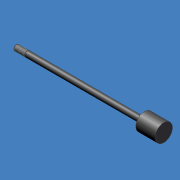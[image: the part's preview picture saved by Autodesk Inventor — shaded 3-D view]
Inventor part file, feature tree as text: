
AUTODESK INVENTOR PART (.ipt)
format: ipt  version: 2012 (Build 160160000, 160)  size: 124,416 bytes
history: native  units: mm (DEFAULTED — no unit token found)
features: other x84, revolve x3, sketch x3, thread x1
ambient origin geometry x8: Origin, YZ Plane, XZ Plane, XY Plane, X Axis, Y Axis, Z Axis, Center Point
bodies: Solid1 (feature_tree)
feature tree (91):
  revolve  "Revolution1"  Angle=360.0deg
  revolve  "Revolution2"  Angle=360.0deg
  thread  "Thread1"  [1 undecoded]
  revolve  "Revolution3"  [1 undecoded]
  other  "rod_cp_XY"
  other  "rod_cp_YZ"
  other  "rod_cp_ZX"
  other  "rod_cp_X"
  other  "rod_cp_Y"
  other  "rod_cp_Z"
  other  "rod_cp_Center"
  other  "to_rod_clevis_XY"
  other  "to_rod_clevis_YZ"
  other  "to_rod_clevis_ZX"
  other  "to_rod_clevis_X"
  other  "to_rod_clevis_Y"
  other  "to_rod_clevis_Z"
  other  "to_rod_clevis_Center"
  other  "rl2_XY"
  other  "rl2_YZ"
  other  "rl2_ZX"
  other  "rl2_X"
  other  "rl2_Y"
  other  "rl2_Z"
  other  "rl2_Center"
  other  "rl1_XY"
  other  "rl1_YZ"
  other  "rl1_ZX"
  other  "rl1_X"
  other  "rl1_Y"
  other  "rl1_Z"
  other  "rl1_Center"
  other  "thd1_XY"
  other  "thd1_YZ"
  other  "thd1_ZX"
  other  "thd1_X"
  other  "thd1_Y"
  other  "thd1_Z"
  other  "thd1_Center"
  other  "thd2_XY"
  other  "thd2_YZ"
  other  "thd2_ZX"
  other  "thd2_X"
  other  "thd2_Y"
  other  "thd2_Z"
  other  "thd2_Center"
  other  "dia1_XY"
  other  "dia1_YZ"
  other  "dia1_ZX"
  other  "dia1_X"
  other  "dia1_Y"
  other  "dia1_Z"
  other  "dia1_Center"
  other  "dia2_XY"
  other  "dia2_YZ"
  other  "dia2_ZX"
  other  "dia2_X"
  other  "dia2_Y"
  other  "dia2_Z"
  other  "dia2_Center"
  other  "dia1r_XY"
  other  "dia1r_YZ"
  other  "dia1r_ZX"
  other  "dia1r_X"
  other  "dia1r_Y"
  other  "dia1r_Z"
  other  "dia1r_Center"
  other  "dia2r_XY"
  other  "dia2r_YZ"
  other  "dia2r_ZX"
  other  "dia2r_X"
  other  "dia2r_Y"
  other  "dia2r_Z"
  other  "dia2r_Center"
  other  "dia12_XY"
  other  "dia12_YZ"
  other  "dia12_ZX"
  other  "dia12_X"
  other  "dia12_Y"
  other  "dia12_Z"
  other  "dia12_Center"
  other  "dia22_XY"
  other  "dia22_YZ"
  other  "dia22_ZX"
  other  "dia22_X"
  other  "dia22_Y"
  other  "dia22_Z"
  other  "dia22_Center"
  sketch  "Sketch_1"  dims[d0=360.0deg d1=360.0deg]
  sketch  "Sketch_3"  dims[d2=12.7mm d3=129.3876mm d4=360.0deg]
  sketch  "Sketch_30"
note: 2 required parameter values undecoded (feature->parameter linkage not recoverable at this tier; creation-order binding heuristic only, values carry confidence <= 0.55)
